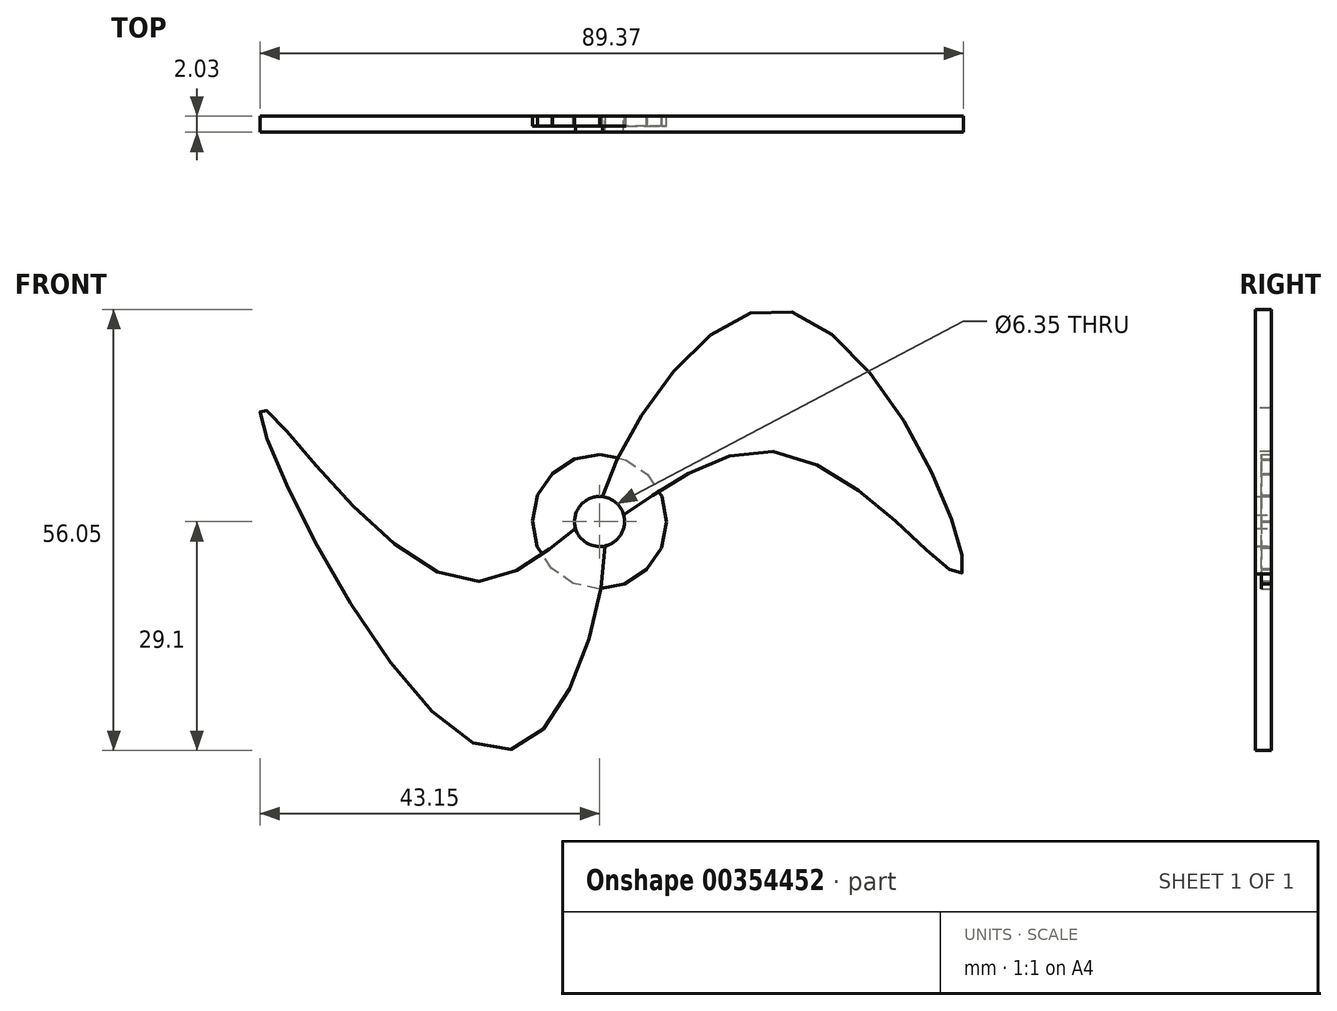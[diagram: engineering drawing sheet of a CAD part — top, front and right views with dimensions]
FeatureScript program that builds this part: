
annotation { "Feature Type Name" : "Feature", "Feature Type Description" : "" }
export const myFeature = defineFeature(function(context is Context, id is Id, definition is map)
    precondition{}
    {
        {
            var Q0;
            Q0=qCreatedBy(makeId("Front.planeOp"),FACE);
            var sketch = newSketch(context, id + "F0", { "sketchPlane" : qUnion([Q0])});
            skCircle(sketch, "E0", {"center": v(0, 0) * mm, "radius": 8.76 * mm});
            skSolve(sketch);
        }
        {
            var Q0;
            Q0=qCreatedBy(makeId("Front.planeOp"),FACE);
            var sketch = newSketch(context, id + "F1", { "sketchPlane" : qUnion([Q0])});
            skFitSpline(sketch, "E1", {"points": [v(0, 0) * mm, v(22.36, 26.94) * mm, v(46.07, -6.47) * mm, v(21.82, 8.9) * mm, v(0, 0) * mm]});
            skFitSpline(sketch, "E2", {"points": [v(0, 0) * mm, v(-12.12, -29.1) * mm, v(-43.1, 14.28) * mm, v(-16.7, -7.54) * mm, v(0, 0) * mm]});
            skSolve(sketch);
        }
        {
            var Q0;
            {var subQ0=sQuery(id+"F1.wireOp",EDGE,"E2");var subQ1=sQuery(id+"F1.wireOp",EDGE,"E1");var subQ2=makeQuery(id+"F1.imprint","INTERSECT",VERTEX,{"disambiguationData":[OD(0.0)],"derivedFrom":[subQ1,subQ0]});Q0=makeQuery(id+"F1.imprint","IMPRINT",FACE,{"disambiguationData":[TD([[makeQuery(id+"F1.imprint","IMPRINT",EDGE,{"disambiguationData":[TD([[subQ2,-1.0]])],"derivedFrom":subQ1}),-1.0]])]});}
            var Q1;
            {var subQ0=sQuery(id+"F1.wireOp",EDGE,"E2");var subQ1=sQuery(id+"F1.wireOp",EDGE,"E1");var subQ2=makeQuery(id+"F1.imprint","INTERSECT",VERTEX,{"disambiguationData":[OD(0.0)],"derivedFrom":[subQ1,subQ0]});Q1=makeQuery(id+"F1.imprint","IMPRINT",FACE,{"disambiguationData":[TD([[makeQuery(id+"F1.imprint","IMPRINT",EDGE,{"disambiguationData":[TD([[subQ2,1.0]])],"derivedFrom":subQ1}),1.0]])]});}
            extrude(context, id + "F2", {"entities" : qUnion([Q0, Q1]), "depth" : 2.03 * mm});
        }
        {
            var Q0;
            Q0=sQuery(id+"F0.wireOp",EDGE,"E0");
            extrude(context, id + "F3", {"bodyType" : ToolBodyType.SURFACE, "surfaceEntities" : qUnion([Q0]), "depth" : 2.54 * mm});
        }
        {
            var Q0;
            Q0=qCreatedBy(makeId("Front.planeOp"),FACE);
            var sketch = newSketch(context, id + "F4", { "sketchPlane" : qUnion([Q0])});
            skCircle(sketch, "E3.cCircle", {"center": v(0, 0) * mm, "radius": 8.37 * mm, "construction": true});
            skLineSegment(sketch, "E3.0", {"start": v(6.1, 5.97) * mm, "end": v(7.92, 3.19) * mm});
            skLineSegment(sketch, "E3.1", {"start": v(7.92, 3.19) * mm, "end": v(8.53, -0.09) * mm});
            skLineSegment(sketch, "E3.2", {"start": v(8.53, -0.09) * mm, "end": v(7.85, -3.34) * mm});
            skLineSegment(sketch, "E3.3", {"start": v(7.85, -3.34) * mm, "end": v(5.97, -6.1) * mm});
            skLineSegment(sketch, "E3.4", {"start": v(5.97, -6.1) * mm, "end": v(3.19, -7.92) * mm});
            skLineSegment(sketch, "E3.5", {"start": v(3.19, -7.92) * mm, "end": v(-0.09, -8.53) * mm});
            skLineSegment(sketch, "E3.6", {"start": v(-0.09, -8.53) * mm, "end": v(-3.34, -7.85) * mm});
            skLineSegment(sketch, "E3.7", {"start": v(-3.34, -7.85) * mm, "end": v(-6.1, -5.97) * mm});
            skLineSegment(sketch, "E3.8", {"start": v(-6.1, -5.97) * mm, "end": v(-7.92, -3.19) * mm});
            skLineSegment(sketch, "E3.9", {"start": v(-7.92, -3.19) * mm, "end": v(-8.53, 0.09) * mm});
            skLineSegment(sketch, "E3.10", {"start": v(-8.53, 0.09) * mm, "end": v(-7.85, 3.34) * mm});
            skLineSegment(sketch, "E3.11", {"start": v(-7.85, 3.34) * mm, "end": v(-5.97, 6.1) * mm});
            skLineSegment(sketch, "E3.12", {"start": v(-5.97, 6.1) * mm, "end": v(-3.19, 7.92) * mm});
            skLineSegment(sketch, "E3.13", {"start": v(-3.19, 7.92) * mm, "end": v(0.09, 8.53) * mm});
            skLineSegment(sketch, "E3.14", {"start": v(0.09, 8.53) * mm, "end": v(3.34, 7.85) * mm});
            skLineSegment(sketch, "E3.15", {"start": v(3.34, 7.85) * mm, "end": v(6.1, 5.97) * mm});
            skPoint(sketch, "E3.0.midPoint", {"position": v(7, 4.58) * mm});
            skSolve(sketch);
        }
        {
            var Q0;
            Q0=makeQuery(id+"F4.imprint","IMPRINT",FACE,{"disambiguationData":[TD([[makeQuery(id+"F4.imprint","IMPRINT",EDGE,{"derivedFrom":sQuery(id+"F4.wireOp",EDGE,"E3.0")}),-1.0]])]});
            extrude(context, id + "F5", {"entities" : qUnion([Q0]), "depth" : 1.27 * mm});
        }
        {
            var Q0;
            Q0=qCreatedBy(makeId("Front.planeOp"),FACE);
            var sketch = newSketch(context, id + "F6", { "sketchPlane" : qUnion([Q0])});
            skPoint(sketch, "E4", {"position": v(0, 0) * mm});
            skSolve(sketch);
        }
        {
            var Q0;
            Q0=sQuery(id+"F6.wireOp",VERTEX,"E4");
            var Q1;
            {var subQ0=sQuery(id+"F1.wireOp",EDGE,"E2");var subQ1=sQuery(id+"F1.wireOp",EDGE,"E1");var subQ2=makeQuery(id+"F1.imprint","INTERSECT",VERTEX,{"disambiguationData":[OD(0.0)],"derivedFrom":[subQ1,subQ0]});Q1=makeQuery(id+"F2.opExtrude","SWEPT_BODY",BODY,{"disambiguationData":[OSD([subQ1,subQ0]),TDD([makeQuery(id+"F1.imprint","IMPRINT",EDGE,{"disambiguationData":[TD([[subQ2,-1.0]])],"derivedFrom":subQ1}),makeQuery(id+"F1.imprint","IMPRINT",EDGE,{"disambiguationData":[TD([[subQ2,-1.0]])],"derivedFrom":subQ0})])]});}
            var Q2;
            {var subQ0=sQuery(id+"F1.wireOp",EDGE,"E2");var subQ1=sQuery(id+"F1.wireOp",EDGE,"E1");var subQ2=makeQuery(id+"F1.imprint","INTERSECT",VERTEX,{"disambiguationData":[OD(0.0)],"derivedFrom":[subQ1,subQ0]});Q2=makeQuery(id+"F2.opExtrude","SWEPT_BODY",BODY,{"disambiguationData":[OSD([subQ1,subQ0]),TDD([makeQuery(id+"F1.imprint","IMPRINT",EDGE,{"disambiguationData":[TD([[subQ2,1.0]])],"derivedFrom":subQ1}),makeQuery(id+"F1.imprint","IMPRINT",EDGE,{"disambiguationData":[TD([[subQ2,1.0]])],"derivedFrom":subQ0})])]});}
            var Q3;
            Q3=makeQuery(id+"F5.opExtrude","SWEPT_BODY",BODY,{"disambiguationData":[OSD([sQuery(id+"F4.wireOp",EDGE,"E3.0"),sQuery(id+"F4.wireOp",EDGE,"E3.1"),sQuery(id+"F4.wireOp",EDGE,"E3.2"),sQuery(id+"F4.wireOp",EDGE,"E3.3"),sQuery(id+"F4.wireOp",EDGE,"E3.4"),sQuery(id+"F4.wireOp",EDGE,"E3.5"),sQuery(id+"F4.wireOp",EDGE,"E3.6"),sQuery(id+"F4.wireOp",EDGE,"E3.7"),sQuery(id+"F4.wireOp",EDGE,"E3.8"),sQuery(id+"F4.wireOp",EDGE,"E3.9"),sQuery(id+"F4.wireOp",EDGE,"E3.10"),sQuery(id+"F4.wireOp",EDGE,"E3.11"),sQuery(id+"F4.wireOp",EDGE,"E3.12"),sQuery(id+"F4.wireOp",EDGE,"E3.13"),sQuery(id+"F4.wireOp",EDGE,"E3.14"),sQuery(id+"F4.wireOp",EDGE,"E3.15")])]});
            hole(context, id + "F7", {"style" : HoleStyle.SIMPLE, "endStyle" : HoleEndStyle.THROUGH, "oppositeDirection" : true, "holeDiameter" : 6.35 * mm, "isTappedThrough" : true, "tappedDepth" : 12.7 * mm, "tapClearance" : 3, "locations" : qUnion([Q0]), "scope" : qUnion([Q1, Q2, Q3])});
        }
    });
